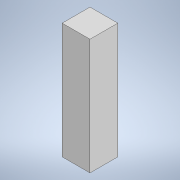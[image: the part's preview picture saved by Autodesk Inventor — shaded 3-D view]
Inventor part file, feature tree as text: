
AUTODESK INVENTOR PART (.ipt)
format: ipt  version: 2022 (Build 260153000, 153)  size: 90,624 bytes
history: native  units: mm
features: extrude x1, sketch x1
ambient origin geometry x8: Origin, YZ Plane, XZ Plane, XY Plane, X Axis, Y Axis, Z Axis, Center Point
bodies: Solid1 (feature_tree)
feature tree (2):
  extrude  "Extrusion1"  Depth=24.4mm
  sketch  "Sketch1"  dims[d0=24.4mm d1=24.4mm d2=101.6mm d3=0.0mm d4=0.5mm d5=0.872665mm]
